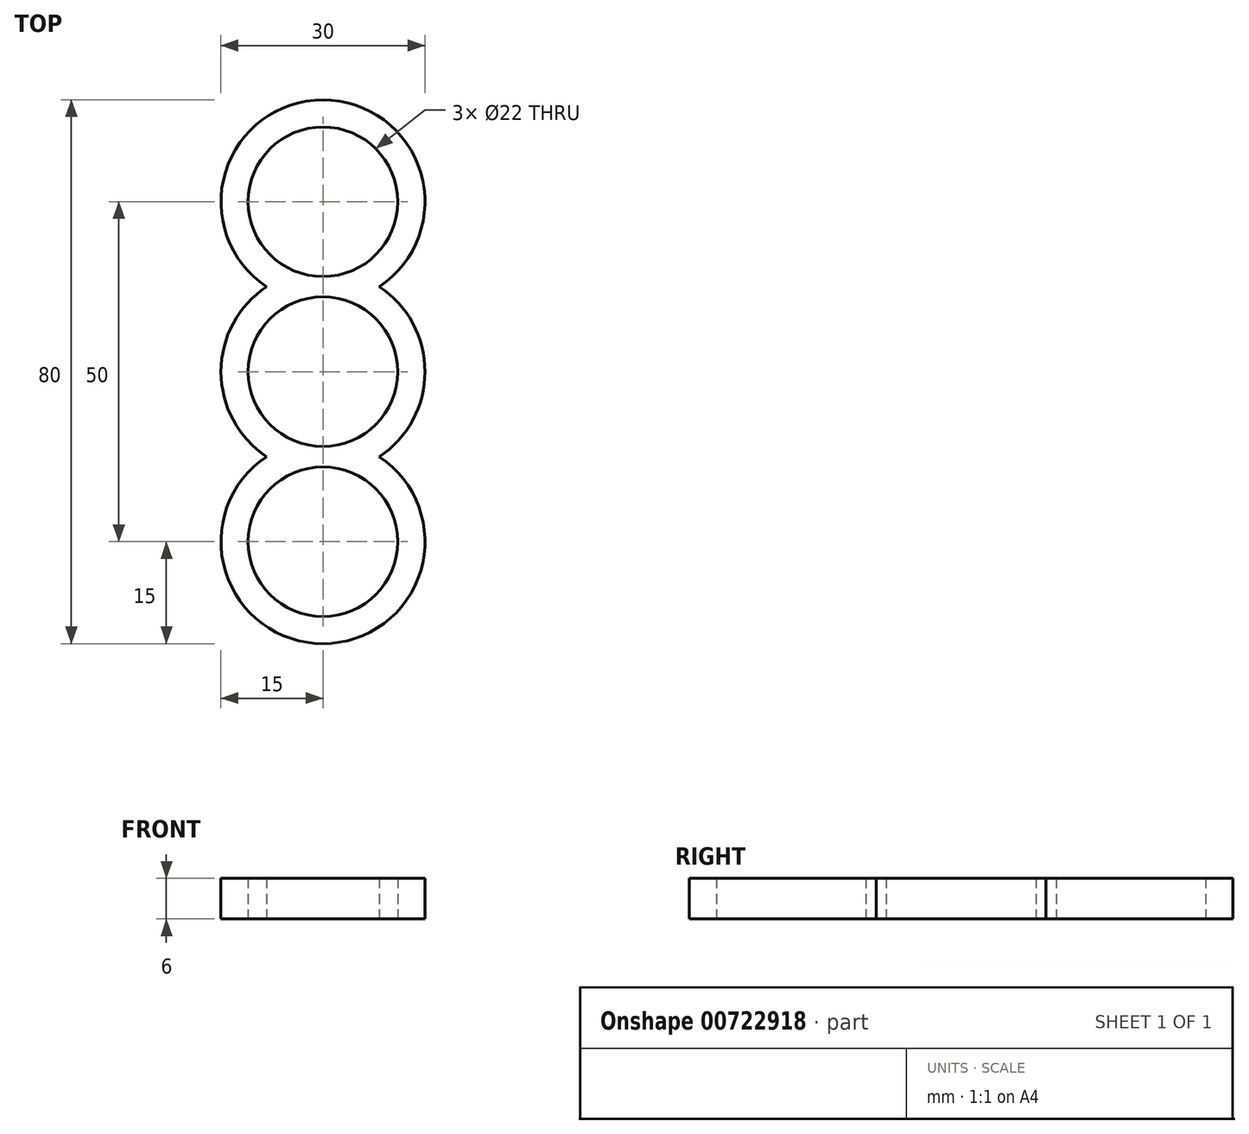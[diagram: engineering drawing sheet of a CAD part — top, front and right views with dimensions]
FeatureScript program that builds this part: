
annotation { "Feature Type Name" : "Feature", "Feature Type Description" : "" }
export const myFeature = defineFeature(function(context is Context, id is Id, definition is map)
    precondition{}
    {
        {
            var Q0;
            Q0=qCreatedBy(makeId("Top.planeOp"),FACE);
            var sketch = newSketch(context, id + "F0", { "sketchPlane" : qUnion([Q0])});
            skCircle(sketch, "E0", {"center": v(0, 0) * mm, "radius": 11 * mm});
            skArc(sketch, "E1", {"start": v(11, -25) * mm, "mid": v(0, -14) * mm, "end": v(-11, -25) * mm});
            skArc(sketch, "E2", {"start": v(-8.3, -12.5) * mm, "mid": v(-13.22, -17.9) * mm, "end": v(-15, -25) * mm});
            skArc(sketch, "E3", {"start": v(8.3, -12.5) * mm, "mid": v(0, 15) * mm, "end": v(-8.3, -12.5) * mm});
            skArc(sketch, "E4.trimOffspring", {"start": v(15, -25) * mm, "mid": v(13.22, -17.9) * mm, "end": v(8.3, -12.5) * mm});
            skArc(sketch, "E5.MirrorCS", {"start": v(8.3, -37.5) * mm, "mid": v(0, -65) * mm, "end": v(-8.3, -37.5) * mm});
            skCircle(sketch, "E6.MirrorC", {"center": v(0, -50) * mm, "radius": 11 * mm});
            skArc(sketch, "E7.MirrorCS", {"start": v(11, -25) * mm, "mid": v(0, -36) * mm, "end": v(-11, -25) * mm});
            skArc(sketch, "E8.MirrorCS", {"start": v(15, -25) * mm, "mid": v(13.22, -32.1) * mm, "end": v(8.3, -37.5) * mm});
            skArc(sketch, "E9.MirrorCS", {"start": v(-8.3, -37.5) * mm, "mid": v(-13.22, -32.1) * mm, "end": v(-15, -25) * mm});
            skSolve(sketch);
        }
        {
            var Q0;
            Q0 = qSketchRegion(id + "F0", true);
            extrude(context, id + "F1", {"entities" : qUnion([Q0]), "depth" : 6 * mm, "offsetDistance" : 25 * mm});
        }
    });
